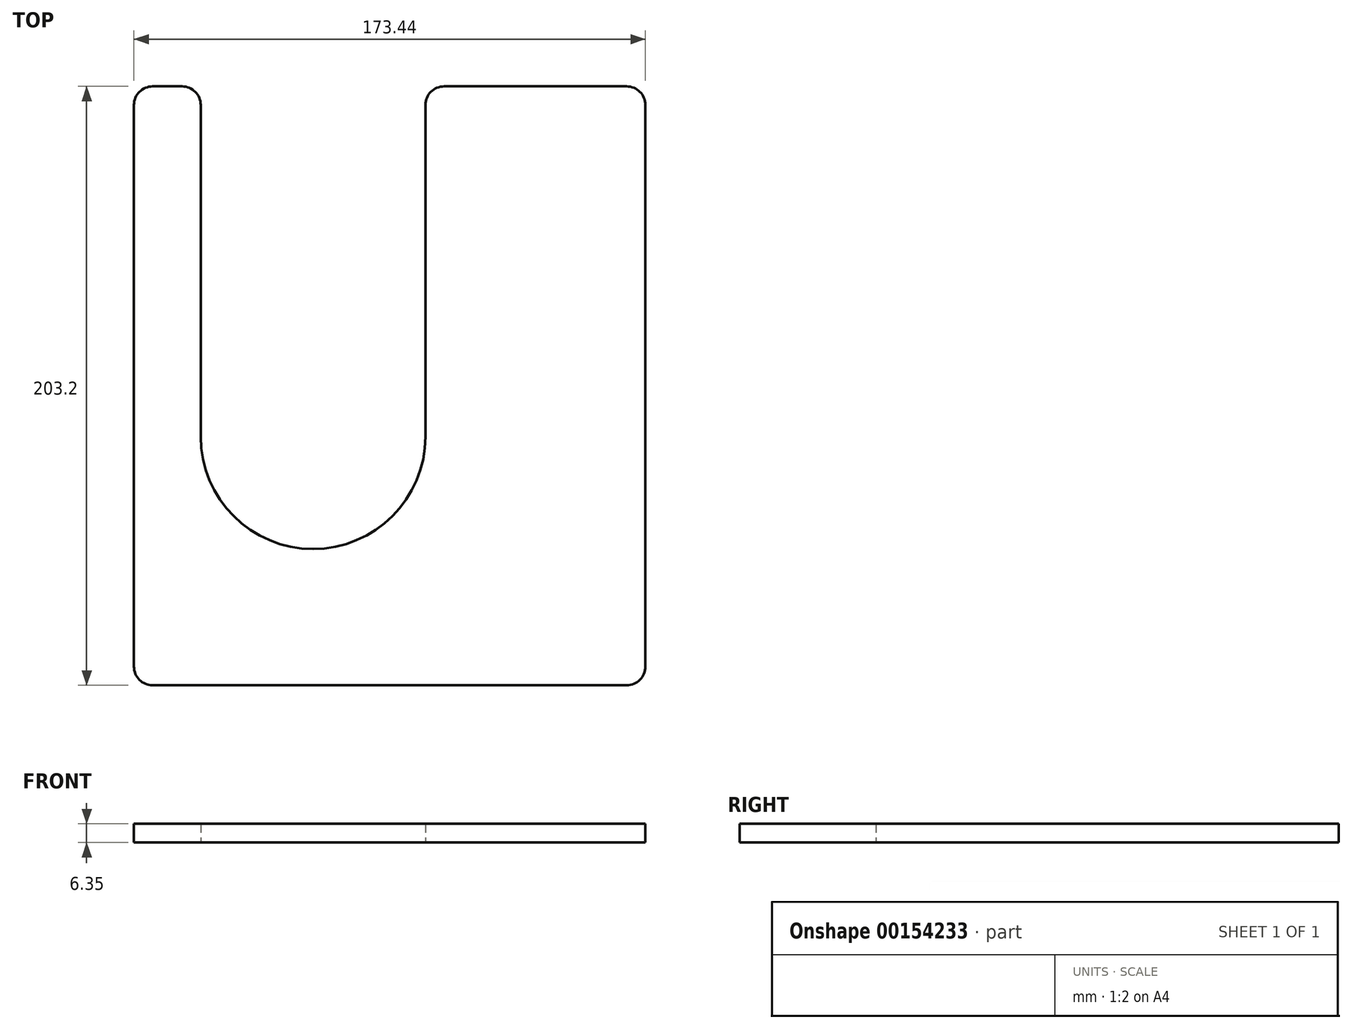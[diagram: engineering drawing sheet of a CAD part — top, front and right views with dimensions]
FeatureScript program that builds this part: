
annotation { "Feature Type Name" : "Feature", "Feature Type Description" : "" }
export const myFeature = defineFeature(function(context is Context, id is Id, definition is map)
    precondition{}
    {
        {
            var Q0;
            Q0=qCreatedBy(makeId("Top.planeOp"),FACE);
            var sketch = newSketch(context, id + "F0", { "sketchPlane" : qUnion([Q0])});
            skLineSegment(sketch, "E0.bottom", {"start": v(-80.37, 101.6) * mm, "end": v(-70.43, 101.6) * mm});
            skLineSegment(sketch, "E0.top", {"start": v(-80.37, -101.6) * mm, "end": v(80.37, -101.6) * mm});
            skLineSegment(sketch, "E0.left", {"start": v(-86.72, 95.25) * mm, "end": v(-86.72, -95.25) * mm});
            skLineSegment(sketch, "E0.right", {"start": v(86.72, 95.25) * mm, "end": v(86.72, -95.25) * mm});
            skPoint(sketch, "E1.visualSharp", {"position": v(-86.72, -101.6) * mm});
            skArc(sketch, "E1.filletArc", {"start": v(-86.72, -95.25) * mm, "mid": v(-84.86, -99.74) * mm, "end": v(-80.37, -101.6) * mm});
            skPoint(sketch, "E2.visualSharp", {"position": v(86.72, -101.6) * mm});
            skArc(sketch, "E2.filletArc", {"start": v(80.37, -101.6) * mm, "mid": v(84.86, -99.74) * mm, "end": v(86.72, -95.25) * mm});
            skPoint(sketch, "E3.visualSharp", {"position": v(86.72, 101.6) * mm});
            skArc(sketch, "E3.filletArc", {"start": v(86.72, 95.25) * mm, "mid": v(84.86, 99.74) * mm, "end": v(80.37, 101.6) * mm});
            skPoint(sketch, "E4.visualSharp", {"position": v(-86.72, 101.6) * mm});
            skArc(sketch, "E4.filletArc", {"start": v(-80.37, 101.6) * mm, "mid": v(-84.86, 99.74) * mm, "end": v(-86.72, 95.25) * mm});
            skLineSegment(sketch, "E5", {"start": v(-64.08, 95.25) * mm, "end": v(-64.08, -17.25) * mm});
            skArc(sketch, "E6", {"start": v(-64.08, -17.25) * mm, "mid": v(-25.98, -55.35) * mm, "end": v(12.12, -17.25) * mm});
            skLineSegment(sketch, "E7", {"start": v(12.12, -17.25) * mm, "end": v(12.12, 95.25) * mm});
            skLineSegment(sketch, "E8.trimOffspring", {"start": v(18.47, 101.6) * mm, "end": v(80.37, 101.6) * mm});
            skPoint(sketch, "E9.visualSharp", {"position": v(-64.08, 101.6) * mm});
            skArc(sketch, "E9.filletArc", {"start": v(-64.08, 95.25) * mm, "mid": v(-65.94, 99.74) * mm, "end": v(-70.43, 101.6) * mm});
            skPoint(sketch, "E10.visualSharp", {"position": v(12.12, 101.6) * mm});
            skArc(sketch, "E10.filletArc", {"start": v(18.47, 101.6) * mm, "mid": v(13.98, 99.74) * mm, "end": v(12.12, 95.25) * mm});
            skSolve(sketch);
        }
        {
            var Q0;
            Q0 = qSketchRegion(id + "F0", true);
            extrude(context, id + "F1", {"entities" : qUnion([Q0]), "depth" : 6.35 * mm});
        }
    });
